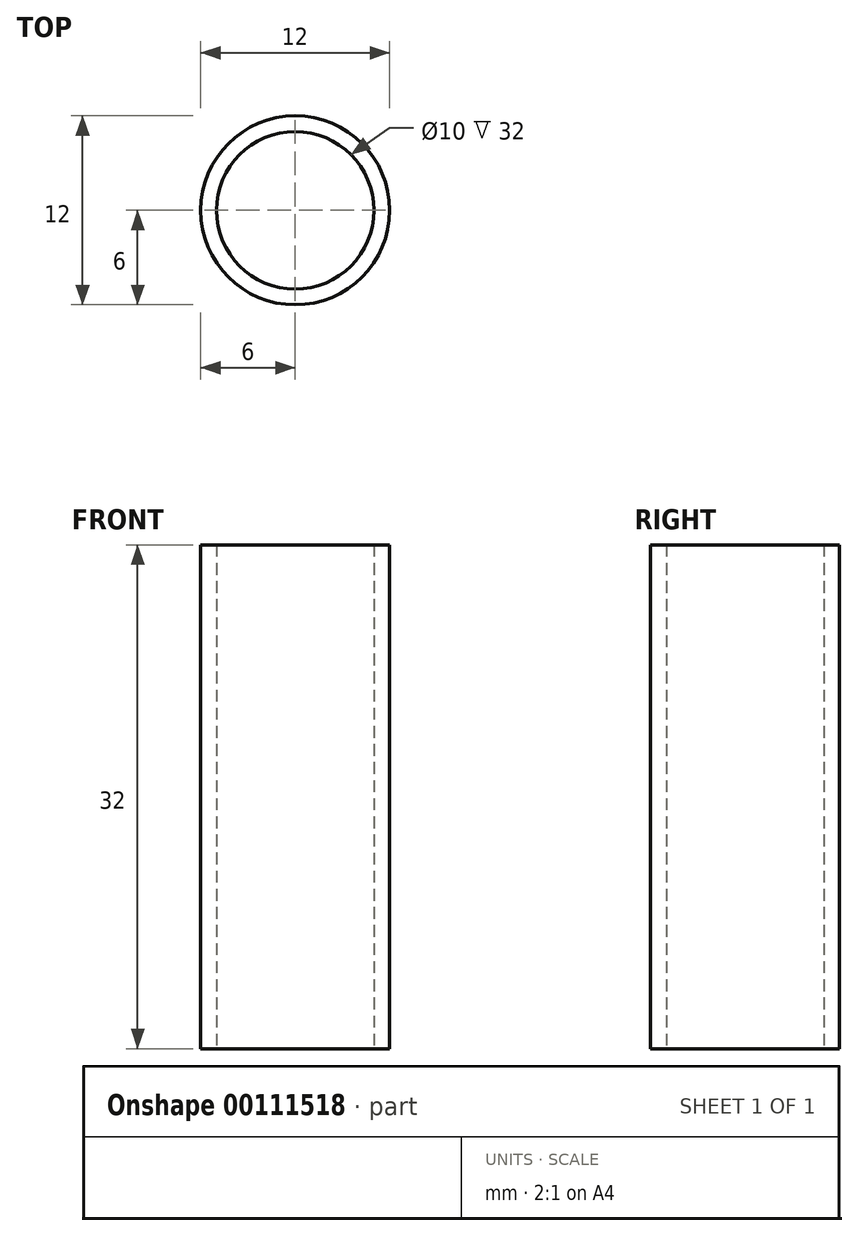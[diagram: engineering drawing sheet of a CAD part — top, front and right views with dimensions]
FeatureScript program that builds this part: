
annotation { "Feature Type Name" : "Feature", "Feature Type Description" : "" }
export const myFeature = defineFeature(function(context is Context, id is Id, definition is map)
    precondition{}
    {
        {
            var Q0;
            Q0=qCreatedBy(makeId("Top.planeOp"),FACE);
            var sketch = newSketch(context, id + "F0", { "sketchPlane" : qUnion([Q0])});
            skCircle(sketch, "E0", {"center": v(0, 0) * mm, "radius": 6 * mm});
            skCircle(sketch, "E1", {"center": v(0, 0) * mm, "radius": 5 * mm});
            skSolve(sketch);
        }
        {
            var Q0;
            Q0=makeQuery(id+"F0.imprint","IMPRINT",FACE,{"disambiguationData":[TD([[makeQuery(id+"F0.imprint","IMPRINT",EDGE,{"derivedFrom":sQuery(id+"F0.wireOp",EDGE,"E0")}),1.0]])]});
            extrude(context, id + "F1", {"entities" : qUnion([Q0]), "depth" : 32 * mm});
        }
    });
